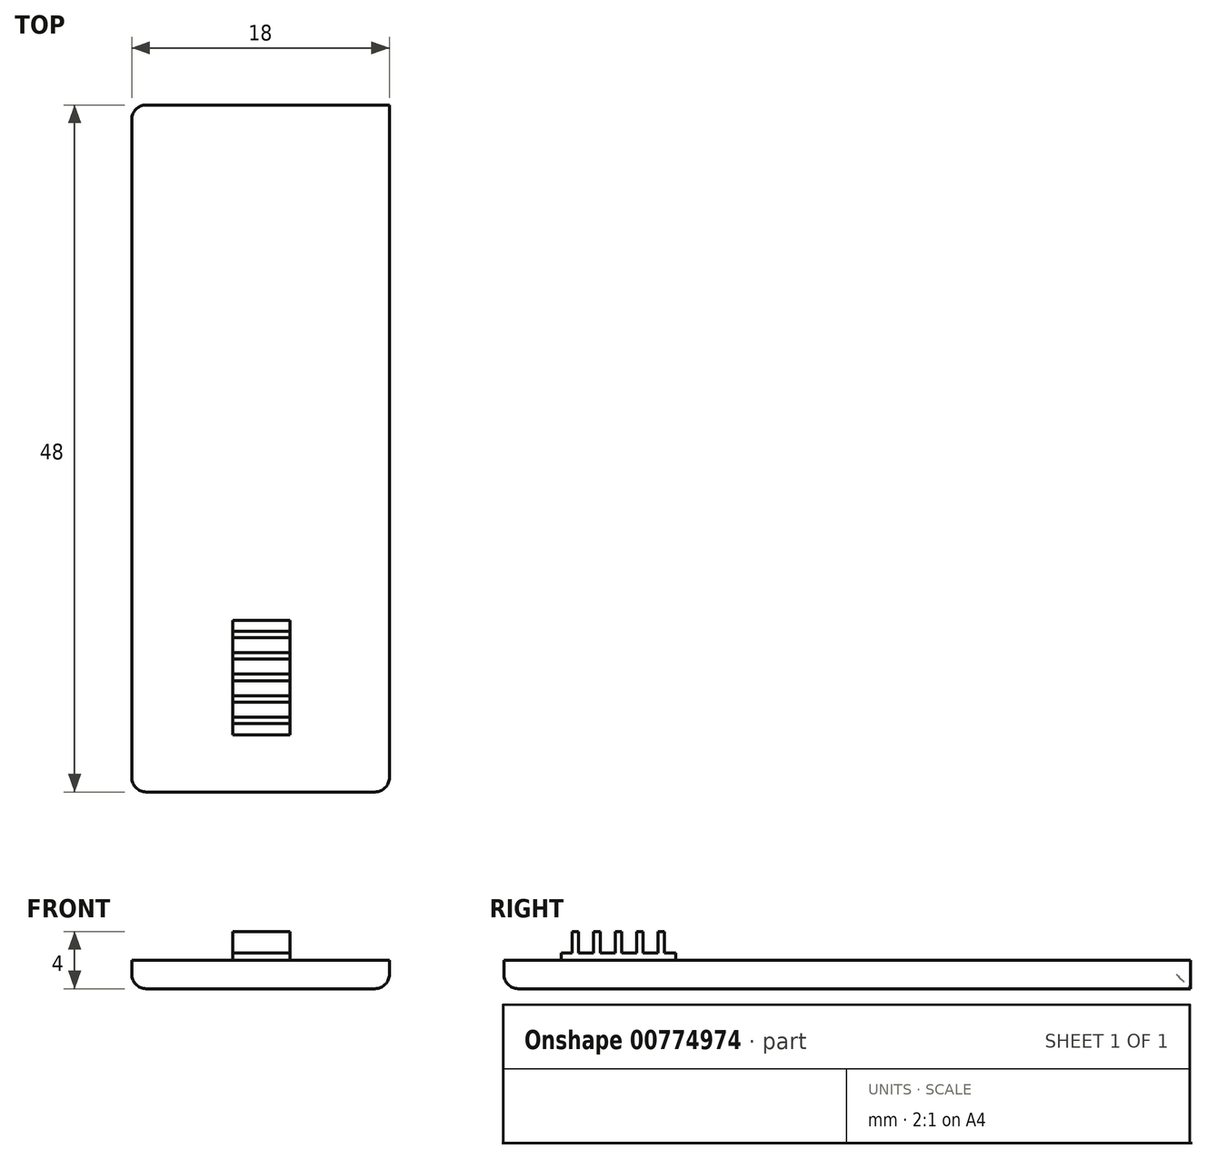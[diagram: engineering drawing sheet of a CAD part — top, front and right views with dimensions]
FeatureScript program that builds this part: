
annotation { "Feature Type Name" : "Feature", "Feature Type Description" : "" }
export const myFeature = defineFeature(function(context is Context, id is Id, definition is map)
    precondition{}
    {
        {
            var Q0;
            Q0=qCreatedBy(makeId("Top.planeOp"),FACE);
            var sketch = newSketch(context, id + "F0", { "sketchPlane" : qUnion([Q0])});
            skPoint(sketch, "E0.middle", {"position": v(0.05, 0) * mm});
            skLineSegment(sketch, "E1.bottom", {"start": v(2.05, -4) * mm, "end": v(-1.95, -4) * mm});
            skLineSegment(sketch, "E1.top", {"start": v(2.05, 4) * mm, "end": v(-1.95, 4) * mm});
            skLineSegment(sketch, "E1.left", {"start": v(2.05, -4) * mm, "end": v(2.05, 4) * mm});
            skLineSegment(sketch, "E1.right", {"start": v(-1.95, -4) * mm, "end": v(-1.95, 4) * mm});
            skLineSegment(sketch, "E2", {"start": v(-1.95, 0.1) * mm, "end": v(-1.95, 0) * mm});
            skPoint(sketch, "E3", {"position": v(0.05, 1.5) * mm});
            skPoint(sketch, "E4", {"position": v(0.05, -1.5) * mm});
            skLineSegment(sketch, "E5.bottom", {"start": v(2.05, -0.23) * mm, "end": v(-1.95, -0.23) * mm});
            skLineSegment(sketch, "E5.top", {"start": v(2.05, 0.22) * mm, "end": v(-1.95, 0.22) * mm});
            skLineSegment(sketch, "E5.left", {"start": v(2.05, -0.23) * mm, "end": v(2.05, 0.22) * mm});
            skLineSegment(sketch, "E5.right", {"start": v(-1.95, -0.23) * mm, "end": v(-1.95, 0.22) * mm});
            skLineSegment(sketch, "E6.bottom", {"start": v(2.05, 1.27) * mm, "end": v(-1.95, 1.27) * mm});
            skLineSegment(sketch, "E6.top", {"start": v(2.05, 1.72) * mm, "end": v(-1.95, 1.72) * mm});
            skLineSegment(sketch, "E6.left", {"start": v(2.05, 1.27) * mm, "end": v(2.05, 1.72) * mm});
            skLineSegment(sketch, "E6.right", {"start": v(-1.95, 1.27) * mm, "end": v(-1.95, 1.72) * mm});
            skLineSegment(sketch, "E7.bottom", {"start": v(2.05, -1.73) * mm, "end": v(-1.95, -1.73) * mm});
            skLineSegment(sketch, "E7.top", {"start": v(2.05, -1.28) * mm, "end": v(-1.95, -1.28) * mm});
            skLineSegment(sketch, "E7.left", {"start": v(2.05, -1.73) * mm, "end": v(2.05, -1.28) * mm});
            skLineSegment(sketch, "E7.right", {"start": v(-1.95, -1.73) * mm, "end": v(-1.95, -1.28) * mm});
            skPoint(sketch, "E8", {"position": v(0.05, 3) * mm});
            skPoint(sketch, "E8.positionSnap0", {"position": v(0.05, 1.27) * mm});
            skPoint(sketch, "E9", {"position": v(0.05, -3) * mm});
            skLineSegment(sketch, "E10.bottom", {"start": v(2.05, -3.23) * mm, "end": v(-1.95, -3.23) * mm});
            skLineSegment(sketch, "E10.top", {"start": v(2.05, -2.78) * mm, "end": v(-1.95, -2.78) * mm});
            skLineSegment(sketch, "E10.left", {"start": v(2.05, -3.23) * mm, "end": v(2.05, -2.78) * mm});
            skLineSegment(sketch, "E10.right", {"start": v(-1.95, -3.23) * mm, "end": v(-1.95, -2.78) * mm});
            skLineSegment(sketch, "E11.bottom", {"start": v(2.05, 2.77) * mm, "end": v(-1.95, 2.77) * mm});
            skLineSegment(sketch, "E11.top", {"start": v(2.05, 3.22) * mm, "end": v(-1.95, 3.22) * mm});
            skLineSegment(sketch, "E11.left", {"start": v(2.05, 2.77) * mm, "end": v(2.05, 3.22) * mm});
            skLineSegment(sketch, "E11.right", {"start": v(-1.95, 2.77) * mm, "end": v(-1.95, 3.22) * mm});
            skLineSegment(sketch, "E12.bottom", {"start": v(-9, 40) * mm, "end": v(9, 40) * mm});
            skLineSegment(sketch, "E12.top", {"start": v(-9, -8) * mm, "end": v(9, -8) * mm});
            skLineSegment(sketch, "E12.left", {"start": v(-9, 40) * mm, "end": v(-9, -8) * mm});
            skLineSegment(sketch, "E12.right", {"start": v(9, 40) * mm, "end": v(9, -8) * mm});
            skSolve(sketch);
        }
        {
            var Q0;
            Q0 = qSketchRegion(id + "F0", true);
            extrude(context, id + "F1", {"entities" : qUnion([Q0]), "depth" : 2 * mm, "offsetDistance" : 25 * mm});
        }
        {
            var Q0;
            {var subQ0=sQuery(id+"F0.wireOp",EDGE,"E1.bottom");Q0=makeQuery(id+"F0.imprint","IMPRINT",FACE,{"disambiguationData":[TD([[makeQuery(id+"F0.imprint","IMPRINT",EDGE,{"derivedFrom":subQ0}),-1.0]])]});}
            var Q1;
            {var subQ0=sQuery(id+"F0.wireOp",EDGE,"E7.bottom");Q1=makeQuery(id+"F0.imprint","IMPRINT",FACE,{"disambiguationData":[TD([[makeQuery(id+"F0.imprint","IMPRINT",EDGE,{"derivedFrom":subQ0}),1.0]])]});}
            var Q2;
            {var subQ0=sQuery(id+"F0.wireOp",EDGE,"E5.bottom");Q2=makeQuery(id+"F0.imprint","IMPRINT",FACE,{"disambiguationData":[TD([[makeQuery(id+"F0.imprint","IMPRINT",EDGE,{"derivedFrom":subQ0}),1.0]])]});}
            var Q3;
            {var subQ0=sQuery(id+"F0.wireOp",EDGE,"E5.top");Q3=makeQuery(id+"F0.imprint","IMPRINT",FACE,{"disambiguationData":[TD([[makeQuery(id+"F0.imprint","IMPRINT",EDGE,{"derivedFrom":subQ0}),-1.0]])]});}
            var Q4;
            {var subQ0=sQuery(id+"F0.wireOp",EDGE,"E6.top");Q4=makeQuery(id+"F0.imprint","IMPRINT",FACE,{"disambiguationData":[TD([[makeQuery(id+"F0.imprint","IMPRINT",EDGE,{"derivedFrom":subQ0}),-1.0]])]});}
            var Q5;
            {var subQ0=sQuery(id+"F0.wireOp",EDGE,"E1.top");Q5=makeQuery(id+"F0.imprint","IMPRINT",FACE,{"disambiguationData":[TD([[makeQuery(id+"F0.imprint","IMPRINT",EDGE,{"derivedFrom":subQ0}),1.0]])]});}
            extrude(context, id + "F2", {"entities" : qUnion([Q0, Q1, Q2, Q3, Q4, Q5]), "operationType" : NewBodyOperationType.ADD, "depth" : 2.5 * mm, "offsetDistance" : 25 * mm});
        }
        {
            var Q0;
            Q0=makeQuery(id+"F0.imprint","IMPRINT",FACE,{"disambiguationData":[TD([[makeQuery(id+"F0.imprint","IMPRINT",EDGE,{"derivedFrom":sQuery(id+"F0.wireOp",EDGE,"E10.bottom")}),-1.0]])]});
            var Q1;
            Q1=makeQuery(id+"F0.imprint","IMPRINT",FACE,{"disambiguationData":[TD([[makeQuery(id+"F0.imprint","IMPRINT",EDGE,{"derivedFrom":sQuery(id+"F0.wireOp",EDGE,"E7.bottom")}),-1.0]])]});
            var Q2;
            {var subQ1=sQuery(id+"F0.wireOp",EDGE,"E5.bottom");Q2=makeQuery(id+"F0.imprint","IMPRINT",FACE,{"disambiguationData":[TD([[makeQuery(id+"F0.imprint","IMPRINT",EDGE,{"derivedFrom":subQ1}),-1.0]])]});}
            var Q3;
            Q3=makeQuery(id+"F0.imprint","IMPRINT",FACE,{"disambiguationData":[TD([[makeQuery(id+"F0.imprint","IMPRINT",EDGE,{"derivedFrom":sQuery(id+"F0.wireOp",EDGE,"E6.bottom")}),-1.0]])]});
            var Q4;
            Q4=makeQuery(id+"F0.imprint","IMPRINT",FACE,{"disambiguationData":[TD([[makeQuery(id+"F0.imprint","IMPRINT",EDGE,{"derivedFrom":sQuery(id+"F0.wireOp",EDGE,"E11.bottom")}),-1.0]])]});
            extrude(context, id + "F3", {"entities" : qUnion([Q0, Q1, Q2, Q3, Q4]), "operationType" : NewBodyOperationType.ADD, "depth" : 4 * mm, "offsetDistance" : 25 * mm});
        }
        {
            var Q0;
            Q0=makeQuery(id+"F1.opExtrude","CAP_EDGE",EDGE,{"disambiguationData":[OSD([sQuery(id+"F0.wireOp",EDGE,"E12.right")])],"isStart":true});
            var Q1;
            Q1=makeQuery(id+"F1.opExtrude","CAP_EDGE",EDGE,{"disambiguationData":[OSD([sQuery(id+"F0.wireOp",EDGE,"E12.left")])],"isStart":true});
            var Q2;
            Q2=makeQuery(id+"F1.opExtrude","CAP_EDGE",EDGE,{"disambiguationData":[OSD([sQuery(id+"F0.wireOp",EDGE,"E12.top")])],"isStart":true});
            var Q3;
            Q3=makeQuery(id+"F1.opExtrude","SWEPT_EDGE",EDGE,{"disambiguationData":[OSD([sQuery(id+"F0.wireOp",EDGE,"E12.bottom"),sQuery(id+"F0.wireOp",EDGE,"E12.left")])]});
            var Q4;
            Q4=makeQuery(id+"F1.opExtrude","SWEPT_EDGE",EDGE,{"disambiguationData":[OSD([sQuery(id+"F0.wireOp",EDGE,"E12.top"),sQuery(id+"F0.wireOp",EDGE,"E12.right")])]});
            var Q5;
            Q5=makeQuery(id+"F1.opExtrude","SWEPT_EDGE",EDGE,{"disambiguationData":[OSD([sQuery(id+"F0.wireOp",EDGE,"E12.top"),sQuery(id+"F0.wireOp",EDGE,"E12.left")])]});
            fillet(context, id + "F4", {"entities" : qUnion([Q0, Q1, Q2, Q3, Q4, Q5]), "radius" : 1 * mm, "tangentPropagation" : true, "allowEdgeOverflow" : false});
        }
    });
